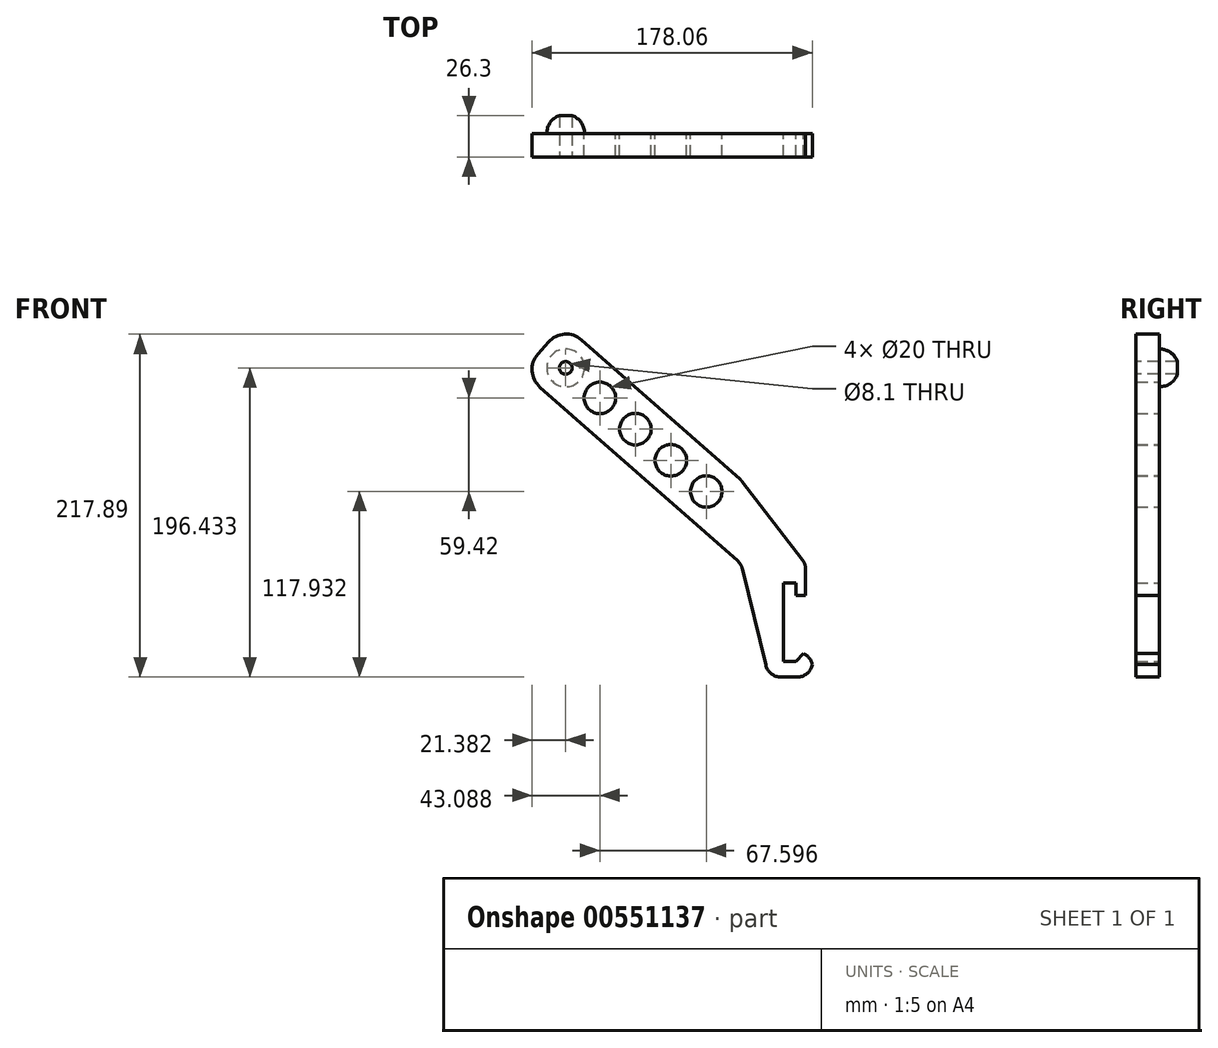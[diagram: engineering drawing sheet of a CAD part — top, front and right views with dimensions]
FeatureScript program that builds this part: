
annotation { "Feature Type Name" : "Feature", "Feature Type Description" : "" }
export const myFeature = defineFeature(function(context is Context, id is Id, definition is map)
    precondition{}
    {
        {
            var Q0;
            Q0=qCreatedBy(makeId("Front.planeOp"),FACE);
            var sketch = newSketch(context, id + "F0", { "sketchPlane" : qUnion([Q0])});
            skLineSegment(sketch, "E0", {"start": v(0, 0) * mm, "end": v(-138.95, 122.14) * mm});
            skLineSegment(sketch, "E1", {"start": v(-138.95, 122.14) * mm, "end": v(-112.54, 152.18) * mm});
            skLineSegment(sketch, "E2", {"start": v(-112.54, 152.18) * mm, "end": v(0, 53.26) * mm});
            skLineSegment(sketch, "E3", {"start": v(41, 0) * mm, "end": v(41, -20) * mm});
            skLineSegment(sketch, "E4", {"start": v(41, -20) * mm, "end": v(35, -20) * mm});
            skLineSegment(sketch, "E5", {"start": v(35, -20) * mm, "end": v(35, -12) * mm});
            skLineSegment(sketch, "E6", {"start": v(35, -12) * mm, "end": v(27, -12) * mm});
            skLineSegment(sketch, "E7", {"start": v(27, -12) * mm, "end": v(27, -62) * mm});
            skLineSegment(sketch, "E8", {"start": v(27, -62) * mm, "end": v(35, -62) * mm});
            skLineSegment(sketch, "E9", {"start": v(35, -62) * mm, "end": v(39.5, -56.88) * mm});
            skLineSegment(sketch, "E10", {"start": v(39.5, -56.88) * mm, "end": v(45.5, -56.88) * mm});
            skLineSegment(sketch, "E11", {"start": v(45.5, -56.88) * mm, "end": v(45.5, -71.88) * mm});
            skLineSegment(sketch, "E12", {"start": v(45.5, -71.88) * mm, "end": v(17.5, -71.88) * mm});
            skLineSegment(sketch, "E13", {"start": v(0, 0) * mm, "end": v(17.5, -71.88) * mm});
            skLineSegment(sketch, "E14", {"start": v(0, 53.26) * mm, "end": v(41, 0) * mm});
            skLineSegment(sketch, "E15", {"start": v(-125.74, 137.16) * mm, "end": v(5.64, 21.67) * mm, "construction": true});
            skCircle(sketch, "E16", {"center": v(-89.7, 105.47) * mm, "radius": 10 * mm});
            skCircle(sketch, "E17", {"center": v(-67.16, 85.67) * mm, "radius": 10 * mm});
            skCircle(sketch, "E18", {"center": v(-44.63, 65.86) * mm, "radius": 10 * mm});
            skCircle(sketch, "E19", {"center": v(-22.1, 46.05) * mm, "radius": 10 * mm});
            skSolve(sketch);
        }
        {
            var Q0;
            Q0=makeQuery(id+"F0.imprint","IMPRINT",FACE,{"disambiguationData":[TD([[makeQuery(id+"F0.imprint","IMPRINT",EDGE,{"derivedFrom":sQuery(id+"F0.wireOp",EDGE,"E0")}),-1.0]])]});
            extrude(context, id + "F1", {"entities" : qUnion([Q0]), "depth" : 15 * mm, "offsetDistance" : 25 * mm});
        }
        {
            var Q0;
            Q0=makeQuery(id+"F1.opExtrude","SWEPT_EDGE",EDGE,{"disambiguationData":[OSD([sQuery(id+"F0.wireOp",EDGE,"E1"),sQuery(id+"F0.wireOp",EDGE,"E2")])]});
            var Q1;
            Q1=makeQuery(id+"F1.opExtrude","SWEPT_EDGE",EDGE,{"disambiguationData":[OSD([sQuery(id+"F0.wireOp",EDGE,"E0"),sQuery(id+"F0.wireOp",EDGE,"E1")])]});
            fillet(context, id + "F2", {"entities" : qUnion([Q0, Q1]), "radius" : 15 * mm, "tangentPropagation" : true, "allowEdgeOverflow" : false});
        }
        {
            var Q0;
            Q0=makeQuery(id+"F1.opExtrude","SWEPT_EDGE",EDGE,{"disambiguationData":[OSD([sQuery(id+"F0.wireOp",EDGE,"E0"),sQuery(id+"F0.wireOp",EDGE,"E13")])]});
            var Q1;
            Q1=makeQuery(id+"F1.opExtrude","SWEPT_EDGE",EDGE,{"disambiguationData":[OSD([sQuery(id+"F0.wireOp",EDGE,"E3"),sQuery(id+"F0.wireOp",EDGE,"E14")])]});
            var Q2;
            Q2=makeQuery(id+"F1.opExtrude","SWEPT_EDGE",EDGE,{"disambiguationData":[OSD([sQuery(id+"F0.wireOp",EDGE,"E2"),sQuery(id+"F0.wireOp",EDGE,"E14")])]});
            var Q3;
            Q3=makeQuery(id+"F1.opExtrude","SWEPT_EDGE",EDGE,{"disambiguationData":[OSD([sQuery(id+"F0.wireOp",EDGE,"E10"),sQuery(id+"F0.wireOp",EDGE,"E11")])]});
            var Q4;
            Q4=makeQuery(id+"F1.opExtrude","SWEPT_EDGE",EDGE,{"disambiguationData":[OSD([sQuery(id+"F0.wireOp",EDGE,"E11"),sQuery(id+"F0.wireOp",EDGE,"E12")])]});
            var Q5;
            Q5=makeQuery(id+"F1.opExtrude","SWEPT_EDGE",EDGE,{"disambiguationData":[OSD([sQuery(id+"F0.wireOp",EDGE,"E12"),sQuery(id+"F0.wireOp",EDGE,"E13")])]});
            fillet(context, id + "F3", {"entities" : qUnion([Q0, Q1, Q2, Q3, Q4, Q5]), "radius" : 10 * mm, "tangentPropagation" : true, "allowEdgeOverflow" : false});
        }
        {
            var Q0;
            Q0=makeQuery(id+"F1.opExtrude","CAP_FACE",FACE,{"disambiguationData":[OSD([sQuery(id+"F0.wireOp",EDGE,"E0"),sQuery(id+"F0.wireOp",EDGE,"E1"),sQuery(id+"F0.wireOp",EDGE,"E2"),sQuery(id+"F0.wireOp",EDGE,"E3"),sQuery(id+"F0.wireOp",EDGE,"E4"),sQuery(id+"F0.wireOp",EDGE,"E5"),sQuery(id+"F0.wireOp",EDGE,"E6"),sQuery(id+"F0.wireOp",EDGE,"E7"),sQuery(id+"F0.wireOp",EDGE,"E8"),sQuery(id+"F0.wireOp",EDGE,"E9"),sQuery(id+"F0.wireOp",EDGE,"E10"),sQuery(id+"F0.wireOp",EDGE,"E11"),sQuery(id+"F0.wireOp",EDGE,"E12"),sQuery(id+"F0.wireOp",EDGE,"E13"),sQuery(id+"F0.wireOp",EDGE,"ZVPSyTwO-NmJR-aiIF-R3QG-YRuaFcbstF5h"),sQuery(id+"F0.wireOp",EDGE,"E14"),sQuery(id+"F0.wireOp",EDGE,"E16"),sQuery(id+"F0.wireOp",EDGE,"E17"),sQuery(id+"F0.wireOp",EDGE,"E18"),sQuery(id+"F0.wireOp",EDGE,"E19")])],"isStart":false});
            var sketch = newSketch(context, id + "F4", { "sketchPlane" : qUnion([Q0])});
            skSolve(sketch);
        }
        {
            var Q0;
            Q0=makeQuery(id+"F1.opExtrude","CAP_FACE",FACE,{"disambiguationData":[OSD([sQuery(id+"F0.wireOp",EDGE,"E0"),sQuery(id+"F0.wireOp",EDGE,"E1"),sQuery(id+"F0.wireOp",EDGE,"E2"),sQuery(id+"F0.wireOp",EDGE,"E3"),sQuery(id+"F0.wireOp",EDGE,"E4"),sQuery(id+"F0.wireOp",EDGE,"E5"),sQuery(id+"F0.wireOp",EDGE,"E6"),sQuery(id+"F0.wireOp",EDGE,"E7"),sQuery(id+"F0.wireOp",EDGE,"E8"),sQuery(id+"F0.wireOp",EDGE,"E9"),sQuery(id+"F0.wireOp",EDGE,"E10"),sQuery(id+"F0.wireOp",EDGE,"E11"),sQuery(id+"F0.wireOp",EDGE,"E12"),sQuery(id+"F0.wireOp",EDGE,"E13"),sQuery(id+"F0.wireOp",EDGE,"E14"),sQuery(id+"F0.wireOp",EDGE,"E16"),sQuery(id+"F0.wireOp",EDGE,"E17"),sQuery(id+"F0.wireOp",EDGE,"E18"),sQuery(id+"F0.wireOp",EDGE,"E19")])],"isStart":true});
            var sketch = newSketch(context, id + "F5", { "sketchPlane" : qUnion([Q0])});
            skCircle(sketch, "E20", {"center": v(111.4, 124.55) * mm, "radius": 12 * mm});
            skLineSegment(sketch, "E21", {"start": v(125.74, 137.16) * mm, "end": v(100.8, 115.23) * mm, "construction": true});
            skSolve(sketch);
        }
        {
            var Q0;
            Q0=makeQuery(id+"F5.imprint","IMPRINT",FACE,{"disambiguationData":[TD([[makeQuery(id+"F5.imprint","IMPRINT",EDGE,{"derivedFrom":sQuery(id+"F5.wireOp",EDGE,"E20")}),1.0]])]});
            extrude(context, id + "F6", {"entities" : qUnion([Q0]), "operationType" : NewBodyOperationType.ADD, "depth" : 12 * mm, "offsetDistance" : 25 * mm});
        }
        {
            var Q0;
            Q0=makeQuery(id+"F6.opExtrude","CAP_EDGE",EDGE,{"disambiguationData":[OSD([sQuery(id+"F5.wireOp",EDGE,"E20")])],"isStart":false});
            fillet(context, id + "F7", {"entities" : qUnion([Q0]), "radius" : 12 * mm, "tangentPropagation" : true, "allowEdgeOverflow" : false});
        }
        {
            var Q0;
            {var subQ15=sQuery(id+"F0.wireOp",EDGE,"E4");Q0=makeQuery(id+"F4.imprint","IMPRINT",FACE,{"disambiguationData":[TD([[makeQuery(id+"F4.imprint","IMPRINT",EDGE,{"derivedFrom":makeQuery(id+"F1.opExtrude","CAP_EDGE",EDGE,{"disambiguationData":[OSD([subQ15])],"isStart":false})}),-1.0]])]});}
            var sketch = newSketch(context, id + "F8", { "sketchPlane" : qUnion([Q0])});
            skCircle(sketch, "E22", {"center": v(-111.4, 124.55) * mm, "radius": 4.05 * mm});
            skSolve(sketch);
        }
        {
            var Q0;
            Q0 = qSketchRegion(id + "F8", true);
            extrude(context, id + "F9", {"entities" : qUnion([Q0]), "operationType" : NewBodyOperationType.REMOVE, "endBound" : BoundingType.THROUGH_ALL, "oppositeDirection" : true, "depth" : 25 * mm, "offsetDistance" : 25 * mm});
        }
    });
